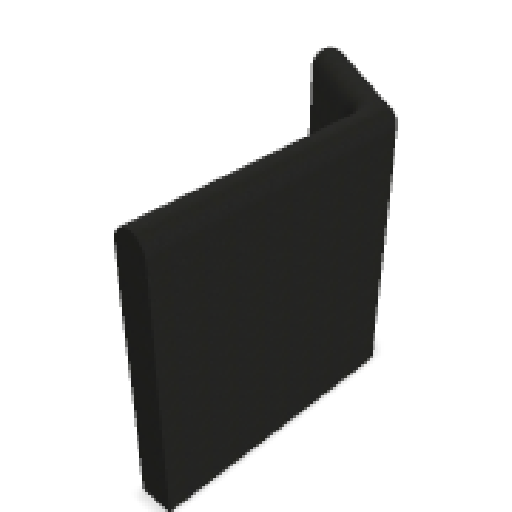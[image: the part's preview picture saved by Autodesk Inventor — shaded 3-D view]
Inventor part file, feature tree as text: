
AUTODESK INVENTOR PART (.ipt)
format: ipt  version: 2023 (Build 270158000, 158)  size: 147,968 bytes
history: native  units: in
note: dims shown in document units (in); Inventor stores cm internally (conversion verified against a paired STEP export)
features: extrude x3, fillet x3, sketch x3, projected_geometry x2
ambient origin geometry x8: Origin, YZ Plane, XZ Plane, XY Plane, X Axis, Y Axis, Z Axis, Center Point
bodies: Solid1 (feature_tree)
feature tree (11):
  extrude  "Extrusion1"  Depth=157.4803in
  extrude  "Extrusion4"  Depth=19.685in
  fillet  "Fillet2"  Radius=2.0in
  fillet  "Fillet3"  Radius=12.0in
  fillet  "Fillet4"  Radius=9.8425in
  extrude  "Extrusion5"  Depth=39.3701in TaperAngle=0.0deg
  sketch  "Sketch1"  dims[d0=19.685in d1=157.4803in]
  sketch  "Sketch2"  dims[d2=118.1102in d3=0.0in d18=19.685in d19=2.0in d20=0.0in d21=12.0in d22=9.8425in]
  projected_geometry  "Projected Loop1"
  sketch  "Sketch4"  dims[d23=9.8425in d24=39.3701in d25=0.0in]
  projected_geometry  "Projected Loop3"
